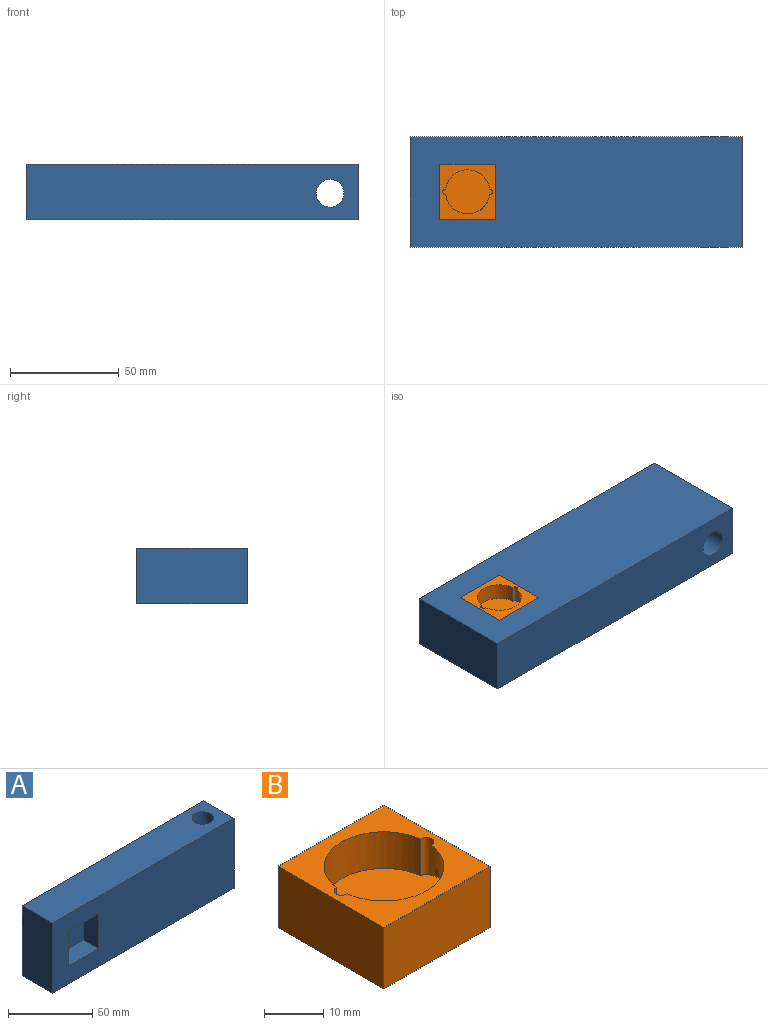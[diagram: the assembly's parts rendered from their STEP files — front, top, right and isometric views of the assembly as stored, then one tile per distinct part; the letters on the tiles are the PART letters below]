
ASSEMBLY  parts=2 mates=1
PART A: 12 faces, bbox 152.4x25.4x50.8 mm
  f0: plane 152.4x50.8mm, normal (0,-1,0), area 7096.8mm2, adj f2,f3,f4,f5,f7,f8,f9,f10
  f1: plane 152.4x50.8mm, normal (0,1,0), area 7741.9mm2, adj f2,f3,f4,f5
  f2: plane 50.8x25.4mm, normal (-1,0,0), area 1290.3mm2, adj f0,f1,f4,f5
  f3: plane 50.8x25.4mm, normal (1,0,0), area 1290.3mm2, adj f0,f1,f4,f5
  f4: plane 152.4x25.4mm, normal (0,0,1), area 3744.3mm2, adj f0,f1,f2,f3,f6
  f5: plane 152.4x25.4mm, normal (0,0,-1), area 3744.3mm2, adj f0,f1,f2,f3,f6
  f6: cylinder r=6.35mm len=50.8mm, axis (0,0,1), area 2026.8mm2, adj f4,f5
  f7: plane 25.4x12.7mm, normal (0,0,-1), area 322.6mm2, adj f0,f8,f10,f11
  f8: plane 25.4x12.7mm, normal (1,0,0), area 322.6mm2, adj f0,f7,f9,f11
  f9: plane 25.4x12.7mm, normal (0,0,1), area 322.6mm2, adj f0,f8,f10,f11
  f10: plane 25.4x12.7mm, normal (-1,0,0), area 322.6mm2, adj f0,f7,f9,f11
  f11: plane 25.4x25.4mm, normal (0,-1,0), area 645.2mm2, adj f7,f8,f9,f10
PART B: 16 faces, bbox 25.4x25.4x12.7 mm
  f0: cylinder r=10.16mm len=20.16mm, axis (0,0,1), area 212.7mm2, adj f1,f7,f9,f10,f11,f13,f14,f15
  f1: cylinder r=1.27mm len=7.62mm, axis (0,0,1), area 23.8mm2, adj f0,f2,f7,f10,f14,f15
  f2: cylinder r=10.16mm len=20.16mm, axis (0,0,1), area 215.7mm2, adj f1,f7,f9,f10,f12,f13
  f3: plane 25.4x12.7mm, normal (0,-1,0), area 322.6mm2, adj f4,f6,f7,f8
  f4: plane 25.4x12.7mm, normal (1,0,0), area 322.6mm2, adj f3,f5,f7,f8
  f5: plane 25.4x12.7mm, normal (0,1,0), area 322.6mm2, adj f4,f6,f7,f8
  f6: plane 25.4x12.7mm, normal (-1,0,0), area 322.6mm2, adj f3,f5,f7,f8
  f7: plane 25.4x25.4mm, normal (0,0,1), area 315.7mm2, adj f0,f1,f2,f3,f4,f5,f6,f9
  f8: plane 25.4x25.4mm, normal (0,0,-1), area 645.2mm2, adj f3,f4,f5,f6
  f9: cylinder r=1.27mm len=3.81mm, axis (0,0,1), area 15.8mm2, adj f0,f2,f7,f11,f12
  f10: plane 23.5x20.32mm, normal (0,0,1), area 337.1mm2, adj f0,f1,f2,f13,f15
  f11: plane 1.07x0.71mm, normal (0,0,-1), area 0.1mm2, adj f0,f9,f13
  f12: plane 4.2x2.16mm, normal (0,0,-1), area 3.4mm2, adj f2,f9,f13
  f13: cylinder r=2.54mm len=4.91mm, axis (0,0,-1), area 25.7mm2, adj f0,f2,f10,f11,f12
  f14: plane 3.77x2.33mm, normal (0,0,-1), area 4.2mm2, adj f0,f1,f15
  f15: cylinder r=2.54mm len=3.81mm, axis (0,0,-1), area 19.3mm2, adj f0,f1,f10,f14
PLACE A rot(axis=(-1,0,0),90deg) t=(-81.07,-49.75,12.67)mm
PLACE B t=(-100.65,-24.27,0.69)mm
MATE fastened A.f11 <-> B.f0  axis (0,0,1) through (-100.65,-24.27,0.69)mm
